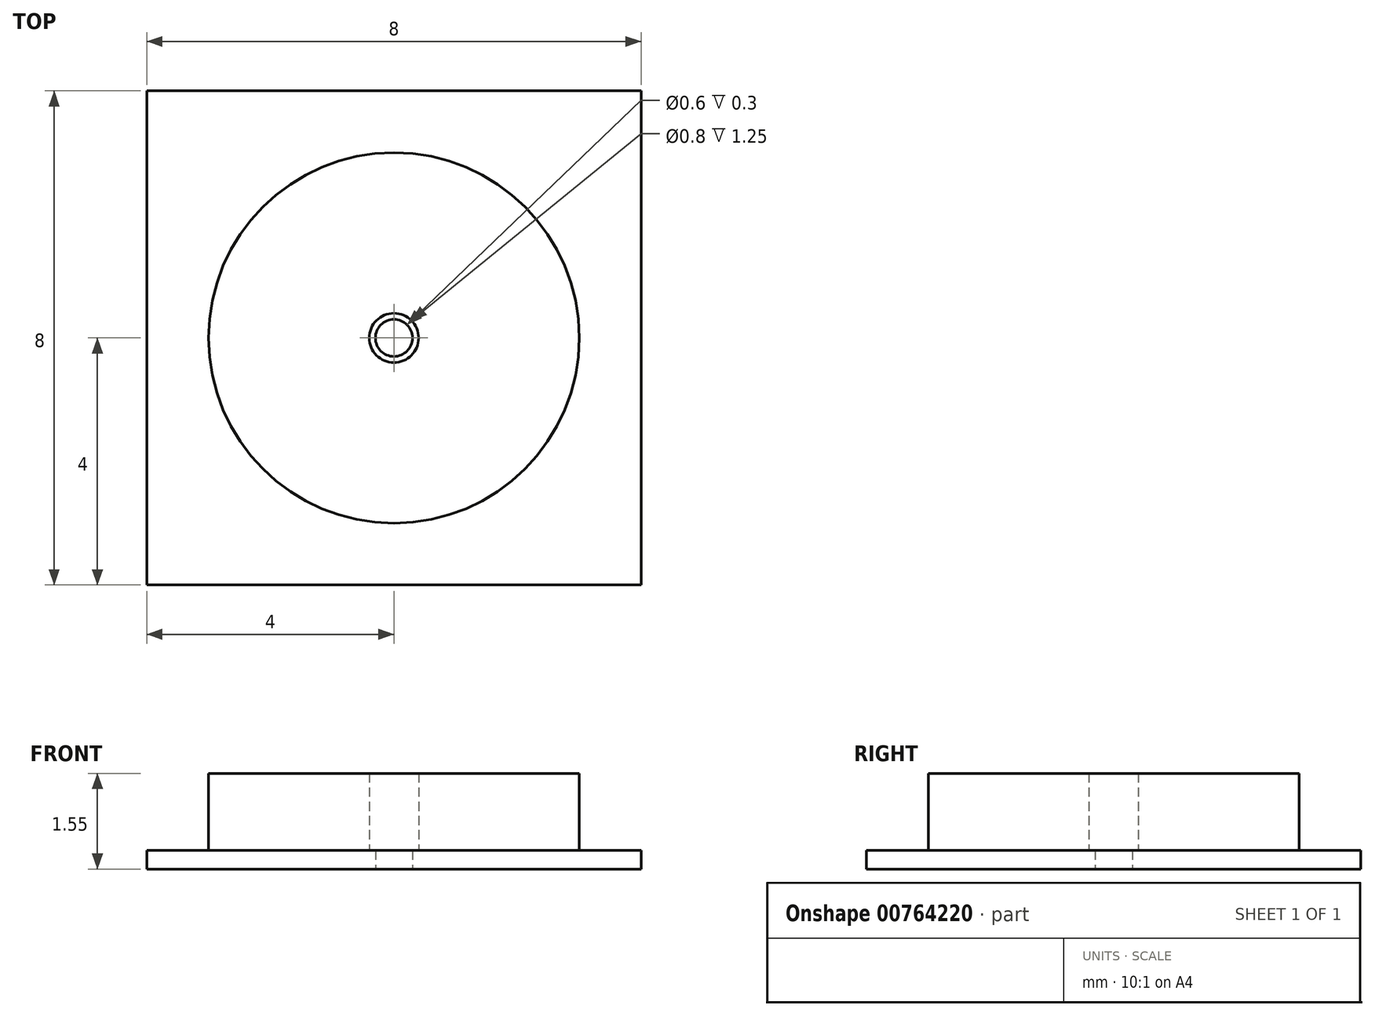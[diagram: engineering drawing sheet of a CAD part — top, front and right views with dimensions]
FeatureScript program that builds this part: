
annotation { "Feature Type Name" : "Feature", "Feature Type Description" : "" }
export const myFeature = defineFeature(function(context is Context, id is Id, definition is map)
    precondition{}
    {
        {
            var Q0;
            Q0=qCreatedBy(makeId("Top.planeOp"),FACE);
            var sketch = newSketch(context, id + "F0", { "sketchPlane" : qUnion([Q0])});
            skLineSegment(sketch, "E0.bottom", {"start": v(4, -4) * mm, "end": v(-4, -4) * mm});
            skLineSegment(sketch, "E0.top", {"start": v(4, 4) * mm, "end": v(-4, 4) * mm});
            skLineSegment(sketch, "E0.left", {"start": v(4, -4) * mm, "end": v(4, 4) * mm});
            skLineSegment(sketch, "E0.right", {"start": v(-4, -4) * mm, "end": v(-4, 4) * mm});
            skPoint(sketch, "E0.middle", {"position": v(0, 0) * mm});
            skCircle(sketch, "E1", {"center": v(0, 0) * mm, "radius": 0.3 * mm});
            skSolve(sketch);
        }
        {
            var Q0;
            Q0 = qSketchRegion(id + "F0", true);
            extrude(context, id + "F1", {"entities" : qUnion([Q0]), "depth" : 0.3 * mm, "offsetDistance" : 25 * mm});
        }
        {
            var Q0;
            Q0=makeQuery(id+"F1.opExtrude","CAP_FACE",FACE,{"disambiguationData":[OSD([sQuery(id+"F0.wireOp",EDGE,"E0.bottom"),sQuery(id+"F0.wireOp",EDGE,"E0.top"),sQuery(id+"F0.wireOp",EDGE,"E0.left"),sQuery(id+"F0.wireOp",EDGE,"E0.right"),sQuery(id+"F0.wireOp",EDGE,"E1")])],"isStart":false});
            var sketch = newSketch(context, id + "F2", { "sketchPlane" : qUnion([Q0])});
            skCircle(sketch, "E2", {"center": v(0, 0) * mm, "radius": 3 * mm});
            skCircle(sketch, "E3", {"center": v(0, 0) * mm, "radius": 0.4 * mm});
            skSolve(sketch);
        }
        {
            var Q0;
            Q0 = qSketchRegion(id + "F2", true);
            extrude(context, id + "F3", {"entities" : qUnion([Q0]), "operationType" : NewBodyOperationType.ADD, "depth" : 1.25 * mm, "offsetDistance" : 25 * mm});
        }
    });
